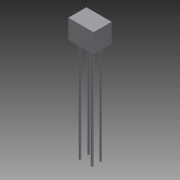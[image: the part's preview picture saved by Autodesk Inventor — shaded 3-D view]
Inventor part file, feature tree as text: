
AUTODESK INVENTOR PART (.ipt)
format: ipt  version: 2011 SP2 (Build 150309200, 309)  size: 87,040 bytes
history: native  units: mm
features: extrude x2, sketch x2
ambient origin geometry x8: Origin, YZ Plane, XZ Plane, XY Plane, X Axis, Y Axis, Z Axis, Center Point
bodies: Solid1 (feature_tree)
feature tree (4):
  extrude  "Extrusion1"  Depth=4.4mm
  extrude  "Extrusion2"  Depth=0.5mm
  sketch  "Sketch1"  dims[d0=6.15mm d1=4.4mm]
  sketch  "Sketch2"  dims[d2=4.7mm d3=0.0mm d4=0.5mm d5=0.5mm d6=0.5mm d7=0.5mm d8=3.44mm d9=3.44mm d10=2.6mm d11=2.6mm d12=1.605mm d13=1.605mm d14=1.605mm d15=1.047mm d16=25.0mm d17=0.0mm]
